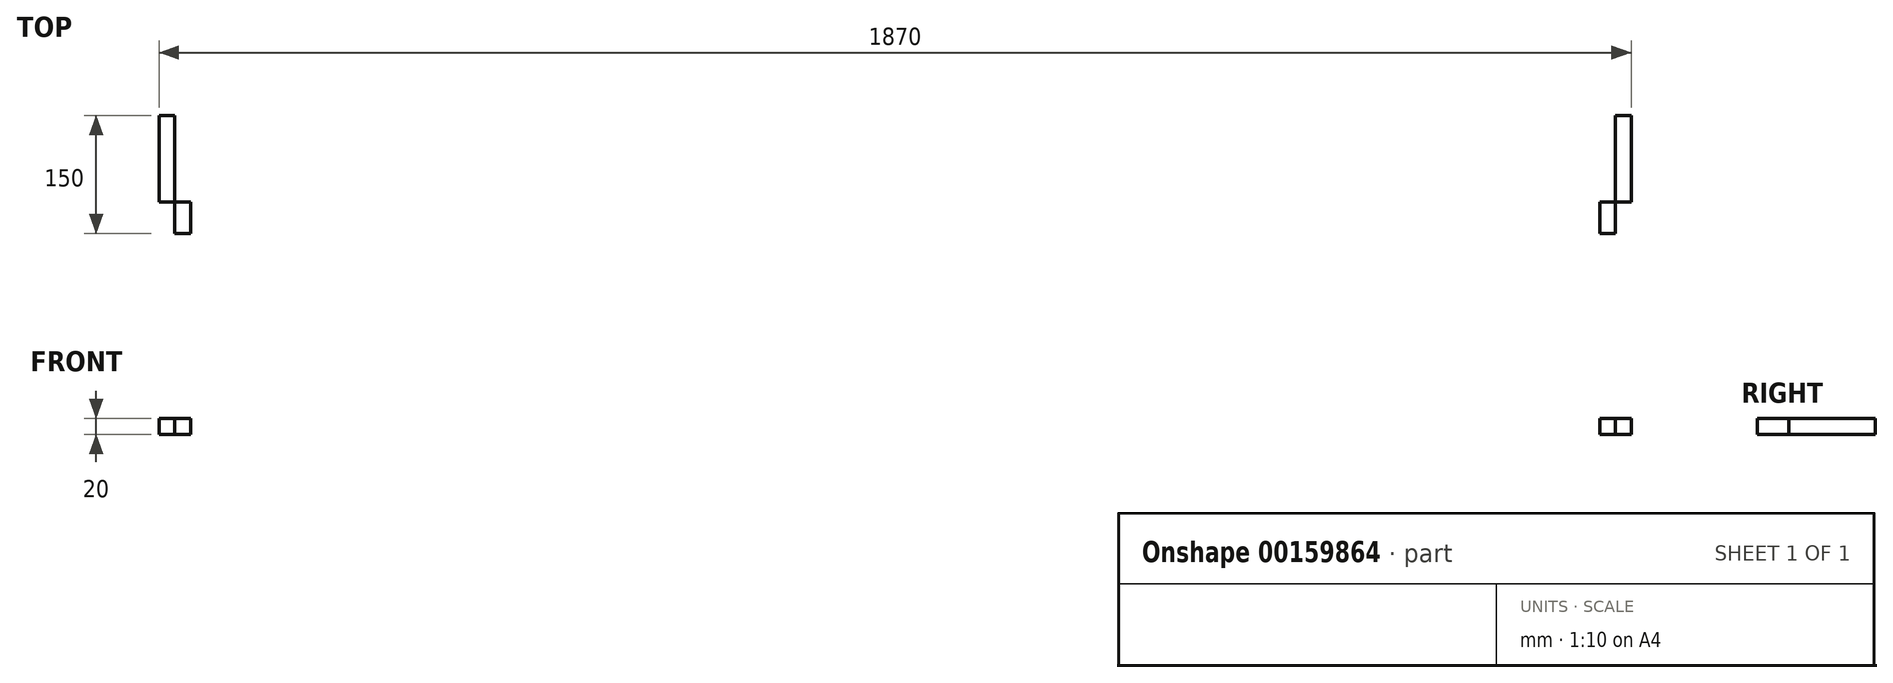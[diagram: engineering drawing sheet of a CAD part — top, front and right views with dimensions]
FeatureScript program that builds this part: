
annotation { "Feature Type Name" : "Feature", "Feature Type Description" : "" }
export const myFeature = defineFeature(function(context is Context, id is Id, definition is map)
    precondition{}
    {
        {
            assignVariable(context, id + "F0", {"name" : "t", "anyValue" : 20 * mm});
        }
        {
            var Q0;
            Q0=qCreatedBy(makeId("Top.planeOp"),FACE);
            var sketch = newSketch(context, id + "F1", { "sketchPlane" : qUnion([Q0])});
            skLineSegment(sketch, "E0.bottom", {"start": v(915, -75) * mm, "end": v(-915, -75) * mm});
            skLineSegment(sketch, "E0.top", {"start": v(915, 75) * mm, "end": v(-915, 75) * mm});
            skLineSegment(sketch, "E0.left", {"start": v(915, -75) * mm, "end": v(915, 75) * mm});
            skLineSegment(sketch, "E0.right", {"start": v(-915, -75) * mm, "end": v(-915, 75) * mm});
            skPoint(sketch, "E0.middle", {"position": v(0, 0) * mm});
            skLineSegment(sketch, "E1.bottom", {"start": v(-915, 75) * mm, "end": v(-935, 75) * mm});
            skLineSegment(sketch, "E1.top", {"start": v(-915, -35) * mm, "end": v(-935, -35) * mm});
            skLineSegment(sketch, "E1.left", {"start": v(-915, 75) * mm, "end": v(-915, -35) * mm});
            skLineSegment(sketch, "E1.right", {"start": v(-935, 75) * mm, "end": v(-935, -35) * mm});
            skLineSegment(sketch, "E2.bottom", {"start": v(915, 75) * mm, "end": v(935, 75) * mm});
            skLineSegment(sketch, "E2.top", {"start": v(915, -35) * mm, "end": v(935, -35) * mm});
            skLineSegment(sketch, "E2.left", {"start": v(915, 75) * mm, "end": v(915, -35) * mm});
            skLineSegment(sketch, "E2.right", {"start": v(935, 75) * mm, "end": v(935, -35) * mm});
            skLineSegment(sketch, "E3.bottom", {"start": v(915, -35) * mm, "end": v(895, -35) * mm});
            skLineSegment(sketch, "E3.top", {"start": v(915, -75) * mm, "end": v(895, -75) * mm});
            skLineSegment(sketch, "E3.left", {"start": v(915, -35) * mm, "end": v(915, -75) * mm});
            skLineSegment(sketch, "E3.right", {"start": v(895, -35) * mm, "end": v(895, -75) * mm});
            skLineSegment(sketch, "E4.bottom", {"start": v(-915, -35) * mm, "end": v(-895, -35) * mm});
            skLineSegment(sketch, "E4.top", {"start": v(-915, -75) * mm, "end": v(-895, -75) * mm});
            skLineSegment(sketch, "E4.left", {"start": v(-915, -35) * mm, "end": v(-915, -75) * mm});
            skLineSegment(sketch, "E4.right", {"start": v(-895, -35) * mm, "end": v(-895, -75) * mm});
            skSolve(sketch);
        }
        {
            var Q0;
            Q0=makeQuery(id+"F1.imprint","IMPRINT",FACE,{"disambiguationData":[TD([[makeQuery(id+"F1.imprint","IMPRINT",EDGE,{"derivedFrom":sQuery(id+"F1.wireOp",EDGE,"E1.bottom")}),1.0]])]});
            var Q1;
            Q1=makeQuery(id+"F1.imprint","IMPRINT",FACE,{"disambiguationData":[TD([[makeQuery(id+"F1.imprint","IMPRINT",EDGE,{"derivedFrom":sQuery(id+"F1.wireOp",EDGE,"E2.bottom")}),-1.0]])]});
            var Q2;
            Q2=makeQuery(id+"F1.imprint","IMPRINT",FACE,{"disambiguationData":[TD([[makeQuery(id+"F1.imprint","IMPRINT",EDGE,{"derivedFrom":sQuery(id+"F1.wireOp",EDGE,"E0.bottom")}),-1.0]])]});
            extrude(context, id + "F2", {"entities" : qUnion([Q0, Q1, Q2]), "oppositeDirection" : true, "depth" : getVariable(context, 't')});
        }
    });
